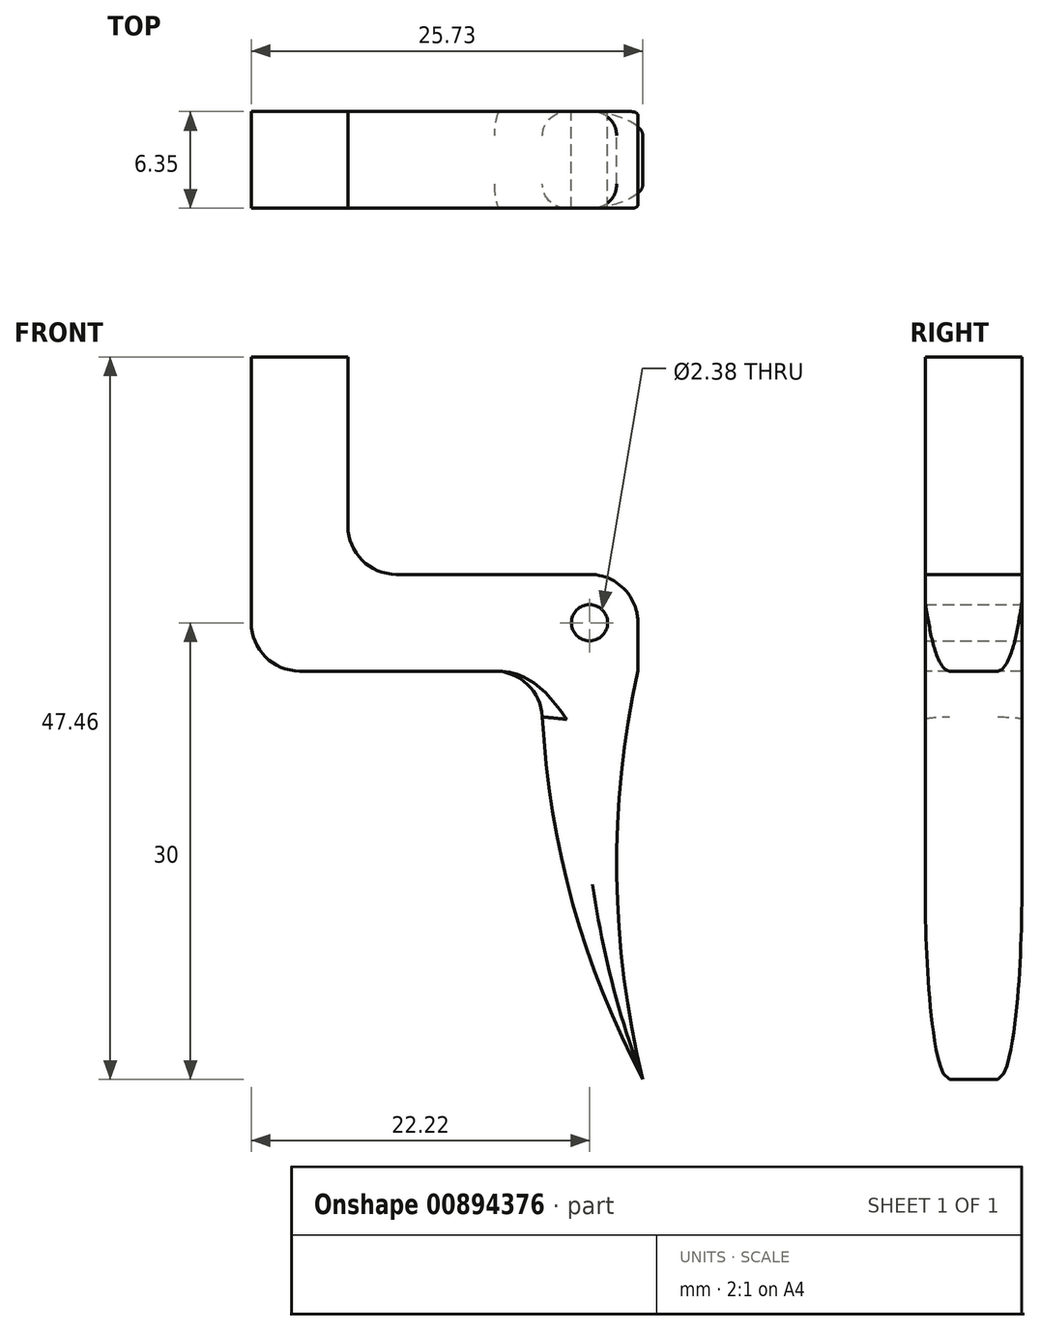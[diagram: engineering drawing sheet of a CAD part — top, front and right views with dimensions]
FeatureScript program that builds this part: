
annotation { "Feature Type Name" : "Feature", "Feature Type Description" : "" }
export const myFeature = defineFeature(function(context is Context, id is Id, definition is map)
    precondition{}
    {
        {
            var Q0;
            Q0=qCreatedBy(makeId("Front.planeOp"),FACE);
            var sketch = newSketch(context, id + "F0", { "sketchPlane" : qUnion([Q0])});
            skLineSegment(sketch, "E0.bottom", {"start": v(14.48, 3.17) * mm, "end": v(-10.92, 3.17) * mm});
            skLineSegment(sketch, "E0.top", {"start": v(14.48, -3.17) * mm, "end": v(-10.92, -3.18) * mm});
            skLineSegment(sketch, "E0.left", {"start": v(14.48, 3.18) * mm, "end": v(14.48, -3.17) * mm});
            skLineSegment(sketch, "E0.right", {"start": v(-10.92, 3.17) * mm, "end": v(-10.92, -3.18) * mm});
            skPoint(sketch, "E0.middle", {"position": v(1.78, 0) * mm});
            skLineSegment(sketch, "E1.bottom", {"start": v(-10.92, 3.17) * mm, "end": v(-4.57, 3.17) * mm});
            skLineSegment(sketch, "E1.top", {"start": v(-10.92, 17.46) * mm, "end": v(-4.57, 17.46) * mm});
            skLineSegment(sketch, "E1.left", {"start": v(-10.92, 3.17) * mm, "end": v(-10.92, 17.46) * mm});
            skLineSegment(sketch, "E1.right", {"start": v(-4.57, 3.17) * mm, "end": v(-4.57, 17.46) * mm});
            skArc(sketch, "E2", {"start": v(8.13, -3.18) * mm, "mid": v(9.82, -17) * mm, "end": v(14.8, -30) * mm});
            skArc(sketch, "E3", {"start": v(14.48, -3.18) * mm, "mid": v(13.09, -16.6) * mm, "end": v(14.8, -30) * mm});
            skPoint(sketch, "E4", {"position": v(11.3, 0) * mm});
            skPoint(sketch, "E5.end.orphan", {"position": v(14.48, 0) * mm});
            skSolve(sketch);
        }
        {
            var Q0;
            Q0=makeQuery(id+"F0.imprint","IMPRINT",FACE,{"disambiguationData":[TD([[makeQuery(id+"F0.imprint","IMPRINT",EDGE,{"derivedFrom":sQuery(id+"F0.wireOp",EDGE,"E1.top")}),-1.0]])]});
            var Q1;
            {var subQ2=sQuery(id+"F0.wireOp",EDGE,"E0.left");Q1=makeQuery(id+"F0.imprint","IMPRINT",FACE,{"disambiguationData":[TD([[makeQuery(id+"F0.imprint","IMPRINT",EDGE,{"derivedFrom":subQ2}),-1.0]])]});}
            var Q2;
            {var subQ0=sQuery(id+"F0.wireOp",EDGE,"E2");Q2=makeQuery(id+"F0.imprint","IMPRINT",FACE,{"disambiguationData":[TD([[makeQuery(id+"F0.imprint","IMPRINT",EDGE,{"derivedFrom":subQ0}),1.0]])]});}
            extrude(context, id + "F1", {"entities" : qUnion([Q0, Q1, Q2]), "depth" : 6.35 * mm, "offsetDistance" : 25.4 * mm});
        }
        {
            var Q0;
            Q0=sQuery(id+"F0.wireOp",VERTEX,"E4");
            var Q1;
            Q1=makeQuery(id+"F1.opExtrude","SWEPT_BODY",BODY,{"disambiguationData":[OSD([sQuery(id+"F0.wireOp",EDGE,"E0.bottom"),sQuery(id+"F0.wireOp",EDGE,"E0.top"),sQuery(id+"F0.wireOp",EDGE,"E0.left"),sQuery(id+"F0.wireOp",EDGE,"E0.right"),sQuery(id+"F0.wireOp",EDGE,"E1.top"),sQuery(id+"F0.wireOp",EDGE,"E1.left"),sQuery(id+"F0.wireOp",EDGE,"E1.right"),sQuery(id+"F0.wireOp",EDGE,"E2"),sQuery(id+"F0.wireOp",EDGE,"E3")])]});
            hole(context, id + "F2", {"style" : HoleStyle.SIMPLE, "endStyle" : HoleEndStyle.BLIND, "oppositeDirection" : true, "holeDiameter" : 2.38 * mm, "majorDiameter" : 6.35 * mm, "holeDepth" : 6.35 * mm, "isTappedThrough" : true, "tappedDepth" : 12.7 * mm, "tapClearance" : 3, "locations" : qUnion([Q0]), "scope" : qUnion([Q1])});
        }
        {
            var Q0;
            Q0=makeQuery(id+"F1.opExtrude","CAP_EDGE",EDGE,{"disambiguationData":[OSD([sQuery(id+"F0.wireOp",EDGE,"E3")])],"isStart":false});
            var Q1;
            Q1=makeQuery(id+"F1.opExtrude","CAP_EDGE",EDGE,{"disambiguationData":[OSD([sQuery(id+"F0.wireOp",EDGE,"E2")])],"isStart":false});
            var Q2;
            Q2=makeQuery(id+"F1.opExtrude","CAP_EDGE",EDGE,{"disambiguationData":[OSD([sQuery(id+"F0.wireOp",EDGE,"E3")])],"isStart":true});
            var Q3;
            Q3=makeQuery(id+"F1.opExtrude","CAP_EDGE",EDGE,{"disambiguationData":[OSD([sQuery(id+"F0.wireOp",EDGE,"E2")])],"isStart":true});
            fillet(context, id + "F3", {"entities" : qUnion([Q0, Q1, Q2, Q3]), "radius" : 1.59 * mm, "tangentPropagation" : true, "allowEdgeOverflow" : false});
        }
        {
            var Q0;
            Q0=makeQuery(id+"F1.opExtrude","SWEPT_EDGE",EDGE,{"disambiguationData":[OSD([sQuery(id+"F0.wireOp",EDGE,"E0.bottom"),sQuery(id+"F0.wireOp",EDGE,"E0.left")])]});
            var Q1;
            Q1=makeQuery(id+"F1.opExtrude","SWEPT_EDGE",EDGE,{"disambiguationData":[OSD([sQuery(id+"F0.wireOp",EDGE,"E0.top"),sQuery(id+"F0.wireOp",EDGE,"E0.right")])]});
            var Q2;
            Q2=makeQuery(id+"F1.opExtrude","SWEPT_EDGE",EDGE,{"disambiguationData":[OSD([sQuery(id+"F0.wireOp",EDGE,"E0.bottom"),sQuery(id+"F0.wireOp",EDGE,"E1.right")])]});
            var Q3;
            Q3=makeQuery(id+"F1.opExtrude","SWEPT_EDGE",EDGE,{"disambiguationData":[OSD([sQuery(id+"F0.wireOp",EDGE,"E0.top"),sQuery(id+"F0.wireOp",EDGE,"E2")])]});
            fillet(context, id + "F4", {"entities" : qUnion([Q0, Q1, Q2, Q3]), "radius" : 3.17 * mm, "tangentPropagation" : true, "allowEdgeOverflow" : false});
        }
    });
